# Revit family: Hager-Volta-IP30-Surface_mounted-syst-NoHosted-PL-pl
name_source: partatom
category: Electrical Equipment
units: mm (PartAtom-declared; Revit-internal decimal feet)

## family parameters
Always vertical = Yes
Cut with Voids When Loaded = No
Panel Configuration = Two Columns, Circuits Across
Part Type = Panelboard
Room Calculation Point = No
Round Connector Dimension = Use Diameter
Shared = No
Work Plane-Based = Yes

## types (8) — shared parameters
Default Elevation = 1219 mm
EF000003 - Sposób montażu = EV000384 - Montaż natynkowy
EF000008 - Szerokość = 305 mm  [stored 1.00066 ft]
EF000049 - Głębokość = 96 mm  [stored 0.314961 ft]
EF000116 - Numer RAL = 9010
EF000118 - Z płytą montażową = No
EF000339 - Rodzaj pokrywy = EV000494 - Brak
EF001062 - Wykonane zgodnie z Dyrektywą Kompatybilności Elektromagnetycznej EMC = No
EF001088 - Możliwość rozbudowy = Yes
EF001134 - Szyna DIN = No
EF002950 - Szerokość wyrażona liczbą modułów = 12
EF005474 - Stopień ochrony (IP) = EV006410 - IP30
EF006244 - Transparentna pokrywa/drzwi = No
EF006306 - Z zamkiem = No
EF009212 - Wykonanie pokrywy = EV009916 - Z otworem
EF015776 - Listwa zaciskowa uziemienia = No
EF015777 - Listwa zaciskowa przewodu neutralnego = No
EF015941 - Drzwi przepuszczające sygnał = No
HG000001 - Liczba kolumn = 1
HG000002 - Z drzwiami lub pokrywą = No
HG000003 - Zakres = Volta
HG000005 - Grubość = 3 mm  [stored 0.00984252 ft]
HG000006 - Montaż podtynkowy = No
HG000009 - Drzwi dwuskrzydłowe = No
HG000010 - Drzwi asymetryczne = No
HG000011 - Puste rzędy od dołu = No
HG000017 - Odległość między biegunami = 18 mm  [stored 0.0590551 ft]
Manufacturer = Hager
Type Comments = Volta
zero-valued in all types: EF000218 - Głębokość wbudowania, EF000332 - Wysokość wbudowania, EF000846 - Szerokość wbudowania, EF001131 - Głębokość wewnętrzna, HG000007 - Liczba pustych kolumn, HG000008 - Liczba pustych rzędów

## per-type parameters (varying)
| type | EF000040 - Wysokość | EF000266 - Liczba rzędów | HG000004 - Referencja producenta | Model |
| Montaż natynkowy IP30 S305 W245 G96.5 12 Jednostki dywizyjne - VA12B | 245 mm | 1 | VA12B | VA12B |
| Montaż natynkowy IP30 S305 W245 G96.5 12 Jednostki dywizyjne - VA12BN | 245 mm | 1 | VA12BN | VA12BN |
| Montaż natynkowy IP30 S305 W370 G96.5 12 Jednostki dywizyjne - VA24B | 370 mm | 2 | VA24B | VA24B |
| Montaż natynkowy IP30 S305 W370 G96.5 12 Jednostki dywizyjne - VA24BN | 370 mm | 2 | VA24BN | VA24BN |
| Montaż natynkowy IP30 S305 W515 G96.5 12 Jednostki dywizyjne - VA36B | 515 mm | 3 | VA36B | VA36B |
| Montaż natynkowy IP30 S305 W515 G96.5 12 Jednostki dywizyjne - VA36BN | 515 mm | 3 | VA36BN | VA36BN |
| Montaż natynkowy IP30 S305 W640 G96.5 12 Jednostki dywizyjne - VA48B | 640 mm  [stored 2.09974 ft] | 4 | VA48B | VA48B |
| Montaż natynkowy IP30 S305 W640 G96.5 12 Jednostki dywizyjne - VA48BN | 640 mm  [stored 2.09974 ft] | 4 | VA48BN | VA48BN |

note: [stored X ft] marks values corroborated as IEEE doubles in the binary element streams (Revit-internal decimal feet)

## geometry (parser evidence)
native form markers: Sweep x13
no freeform markers — native parametric forms only
